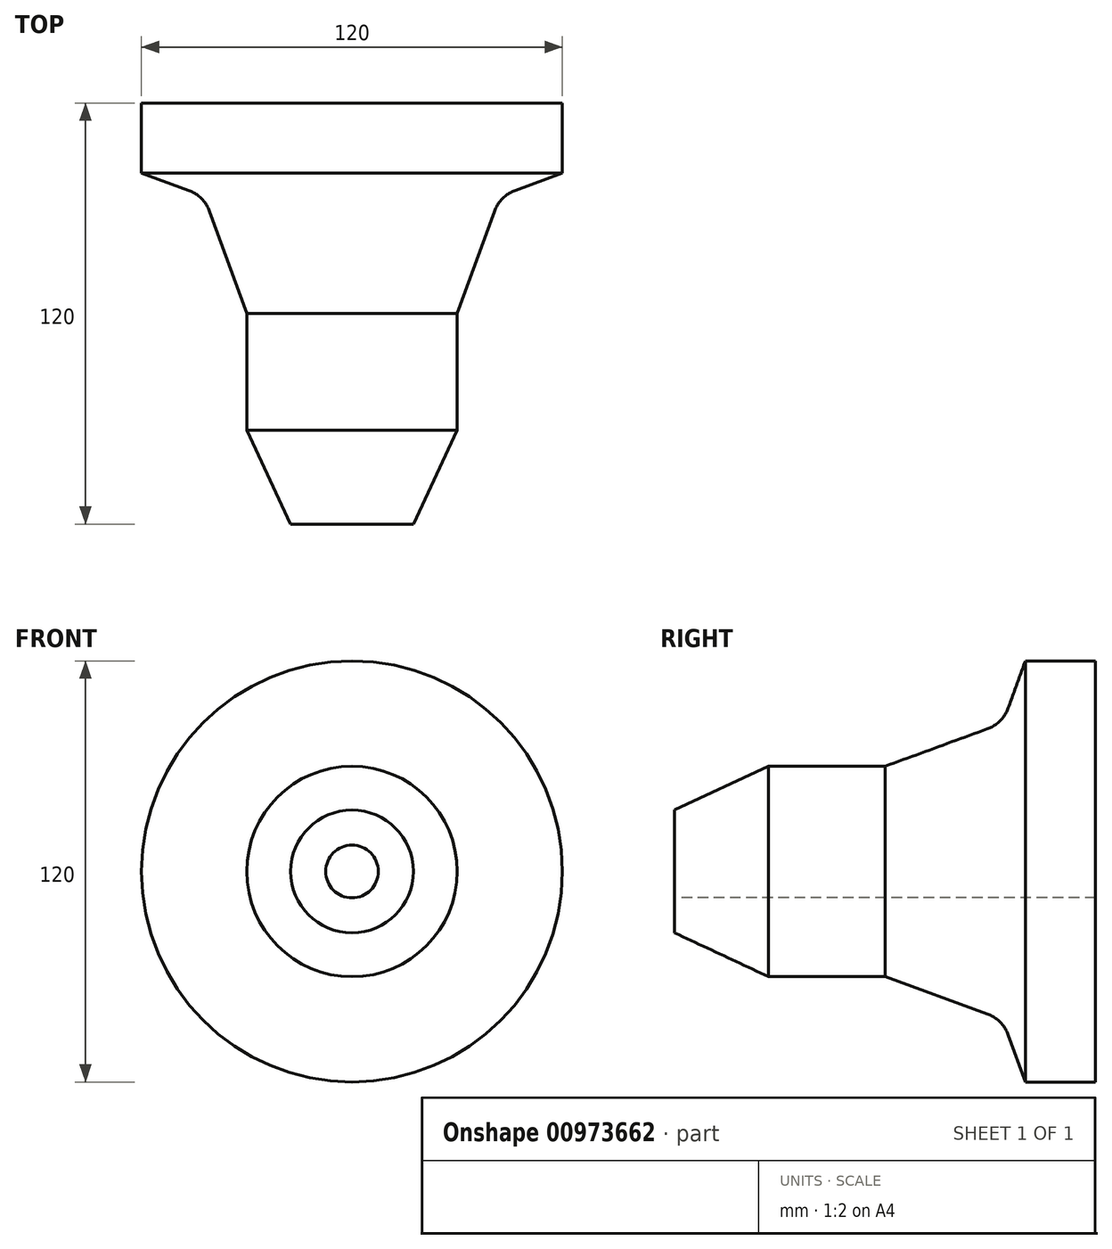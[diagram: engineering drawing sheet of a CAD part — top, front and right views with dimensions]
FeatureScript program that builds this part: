
annotation { "Feature Type Name" : "Feature", "Feature Type Description" : "" }
export const myFeature = defineFeature(function(context is Context, id is Id, definition is map)
    precondition{}
    {
        {
            var Q0;
            Q0=qCreatedBy(makeId("Right.planeOp"),FACE);
            var sketch = newSketch(context, id + "F0", { "sketchPlane" : qUnion([Q0])});
            skLineSegment(sketch, "E0", {"start": v(0, 0) * mm, "end": v(103.45, 0) * mm, "construction": true});
            skLineSegment(sketch, "E1", {"start": v(0, 7.5) * mm, "end": v(120, 7.5) * mm});
            skLineSegment(sketch, "E2", {"start": v(0, 7.5) * mm, "end": v(0, 17.5) * mm});
            skLineSegment(sketch, "E3", {"start": v(0, 17.5) * mm, "end": v(26.8, 30) * mm});
            skLineSegment(sketch, "E4", {"start": v(26.8, 30) * mm, "end": v(60, 30) * mm});
            skLineSegment(sketch, "E5", {"start": v(60, 30) * mm, "end": v(93.52, 42.2) * mm});
            skLineSegment(sketch, "E6", {"start": v(120, 7.5) * mm, "end": v(120, 60) * mm});
            skLineSegment(sketch, "E7", {"start": v(93.52, 42.2) * mm, "end": v(100, 60) * mm});
            skLineSegment(sketch, "E8", {"start": v(100, 60) * mm, "end": v(120, 60) * mm});
            skSolve(sketch);
        }
        {
            var Q0;
            Q0=makeQuery(id+"F0.imprint","IMPRINT",FACE,{"disambiguationData":[TD([[makeQuery(id+"F0.imprint","IMPRINT",EDGE,{"derivedFrom":sQuery(id+"F0.wireOp",EDGE,"E1")}),1.0]])]});
            var Q1;
            Q1=sQuery(id+"F0.wireOp",EDGE,"E0");
            revolve(context, id + "F1", {"surfaceOperationType" : NewSurfaceOperationType.NEW, "entities" : qUnion([Q0]), "axis" : qUnion([Q1]), "revolveType" : RevolveType.FULL});
        }
        {
            var Q0;
            Q0=makeQuery(id+"F1.opRevolve","SWEPT_EDGE",EDGE,{"disambiguationData":[OSD([sQuery(id+"F0.wireOp",EDGE,"E5"),sQuery(id+"F0.wireOp",EDGE,"E7")])]});
            fillet(context, id + "F2", {"entities" : qUnion([Q0]), "radius" : 10 * mm, "tangentPropagation" : true, "allowEdgeOverflow" : false});
        }
    });
